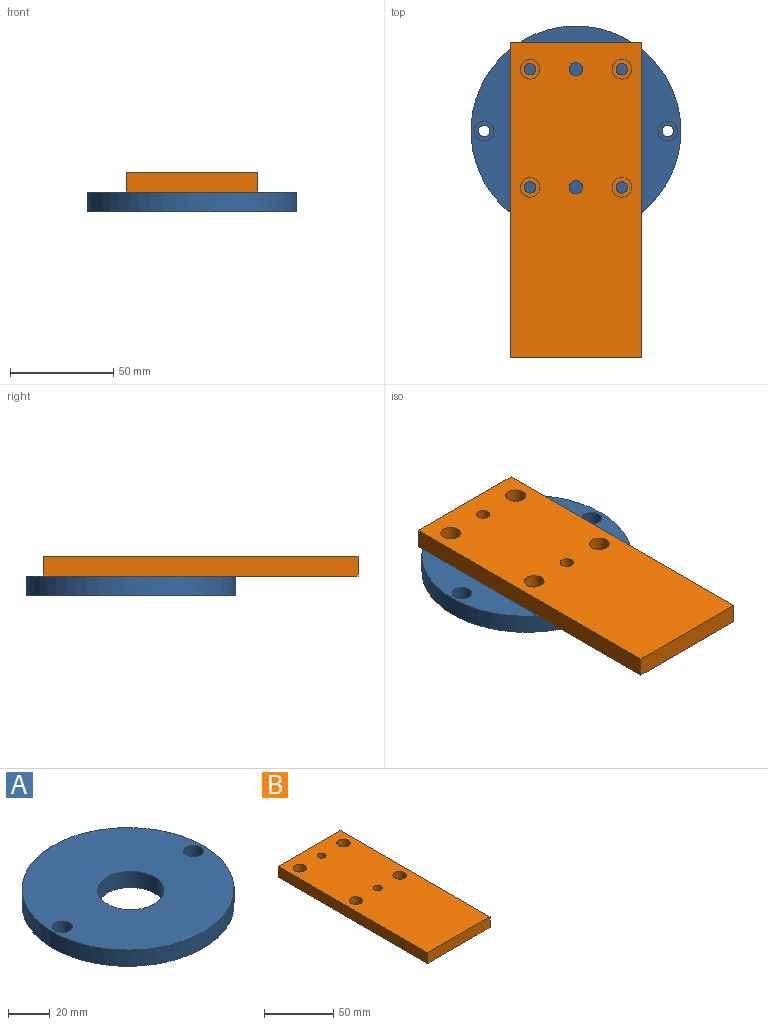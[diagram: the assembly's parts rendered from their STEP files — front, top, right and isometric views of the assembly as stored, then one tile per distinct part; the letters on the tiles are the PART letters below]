
ASSEMBLY  parts=2 mates=1
PART A: 10 faces, bbox 101.6x101.6x9.5 mm
  f0: cylinder r=2.78mm len=5.56mm, axis (0,0,1), area 55.4mm2, adj f4,f7
  f1: cylinder r=2.78mm len=5.56mm, axis (0,0,1), area 55.4mm2, adj f4,f5
  f2: cylinder r=50.8mm len=101.6mm, axis (0,0,-1), area 3040.2mm2, adj f3,f4
  f3: plane 101.6x101.6mm, normal (0,0,1), area 7173.1mm2, adj f2,f6,f8,f9
  f4: plane 101.6x101.6mm, normal (0,0,-1), area 7267.1mm2, adj f0,f1,f2,f9
  f5: plane 9.53x9.53mm, normal (0,0,1), area 47mm2, adj f1,f6
  f6: cylinder r=4.76mm len=9.53mm, axis (0,0,1), area 190mm2, adj f3,f5
  f7: plane 9.53x9.53mm, normal (0,0,1), area 47mm2, adj f0,f8
  f8: cylinder r=4.76mm len=9.53mm, axis (0,0,1), area 190mm2, adj f3,f7
  f9: cylinder r=15.88mm len=31.75mm, axis (0,0,1), area 950.1mm2, adj f3,f4
PART B: 20 faces, bbox 63.5x152.4x9.5 mm
  f0: cylinder r=2.77mm len=5.54mm, axis (0,0,1), area 55.2mm2, adj f5,f18
  f1: cylinder r=2.77mm len=5.54mm, axis (0,0,1), area 55.2mm2, adj f5,f16
  f2: cylinder r=2.77mm len=5.54mm, axis (0,0,1), area 55.2mm2, adj f5,f14
  f3: cylinder r=2.77mm len=5.54mm, axis (0,0,1), area 55.2mm2, adj f5,f12
  f4: plane 152.4x9.53mm, normal (-1,0,0), area 1451.6mm2, adj f5,f7,f8,f9
  f5: plane 152.4x63.5mm, normal (0,0,-1), area 9517.7mm2, adj f0,f1,f2,f3,f4,f6,f8,f9
  f6: plane 152.4x9.53mm, normal (1,0,0), area 1451.6mm2, adj f5,f7,f8,f9
  f7: plane 152.4x63.5mm, normal (0,0,1), area 9329mm2, adj f4,f6,f8,f9,f10,f11,f13,f15
  f8: plane 63.5x9.53mm, normal (0,1,0), area 604.8mm2, adj f4,f5,f6,f7
  f9: plane 63.5x9.53mm, normal (0,-1,0), area 604.8mm2, adj f4,f5,f6,f7
  f10: cylinder r=3.17mm len=9.53mm, axis (0,0,1), area 190mm2, adj f5,f7
  f11: cylinder r=3.17mm len=9.53mm, axis (0,0,1), area 190mm2, adj f5,f7
  f12: plane 9.53x9.53mm, normal (0,0,1), area 47.2mm2, adj f3,f13
  f13: cylinder r=4.76mm len=9.53mm, axis (0,0,1), area 190mm2, adj f7,f12
  f14: plane 9.53x9.53mm, normal (0,0,1), area 47.2mm2, adj f2,f15
  f15: cylinder r=4.76mm len=9.53mm, axis (0,0,1), area 190mm2, adj f7,f14
  f16: plane 9.53x9.53mm, normal (0,0,1), area 47.2mm2, adj f1,f17
  f17: cylinder r=4.76mm len=9.53mm, axis (0,0,1), area 190mm2, adj f7,f16
  f18: plane 9.53x9.53mm, normal (0,0,1), area 47.2mm2, adj f0,f19
  f19: cylinder r=4.76mm len=9.53mm, axis (0,0,1), area 190mm2, adj f7,f18
PLACE A t=(-0.01,0.02,-4.72)mm fixed
PLACE B t=(-31.76,-109.84,4.8)mm
MATE fastened B.f5 <-> A.f9  axis (0,0,-1) through (-0.01,-1.89,4.8)mm
